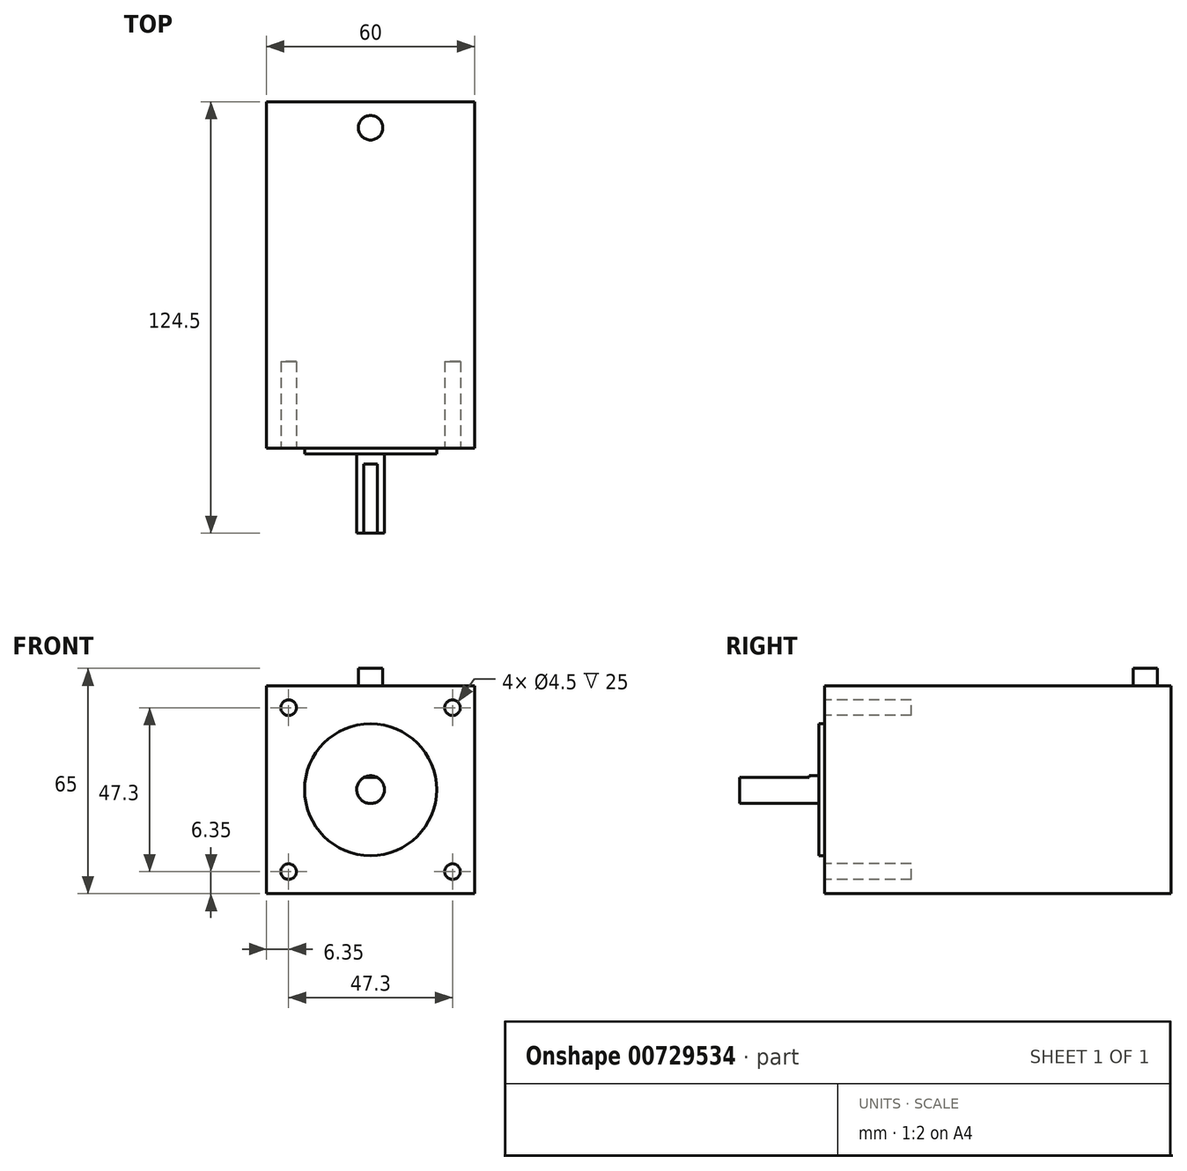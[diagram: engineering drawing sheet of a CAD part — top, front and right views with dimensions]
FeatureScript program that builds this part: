
annotation { "Feature Type Name" : "Feature", "Feature Type Description" : "" }
export const myFeature = defineFeature(function(context is Context, id is Id, definition is map)
    precondition{}
    {
        {
            var Q0;
            Q0=qCreatedBy(makeId("Front.planeOp"),FACE);
            var sketch = newSketch(context, id + "F0", { "sketchPlane" : qUnion([Q0])});
            skLineSegment(sketch, "E0.bottom", {"start": v(-30, 30) * mm, "end": v(30, 30) * mm});
            skLineSegment(sketch, "E0.top", {"start": v(-30, -30) * mm, "end": v(30, -30) * mm});
            skLineSegment(sketch, "E0.left", {"start": v(-30, 30) * mm, "end": v(-30, -30) * mm});
            skLineSegment(sketch, "E0.right", {"start": v(30, 30) * mm, "end": v(30, -30) * mm});
            skPoint(sketch, "E0.middle", {"position": v(0, 0) * mm});
            skCircle(sketch, "E1", {"center": v(0, 0) * mm, "radius": 19.05 * mm});
            skLineSegment(sketch, "E2.bottom", {"start": v(-23.65, 23.65) * mm, "end": v(23.65, 23.65) * mm, "construction": true});
            skLineSegment(sketch, "E2.top", {"start": v(-23.65, -23.65) * mm, "end": v(23.65, -23.65) * mm, "construction": true});
            skLineSegment(sketch, "E2.left", {"start": v(-23.65, 23.65) * mm, "end": v(-23.65, -23.65) * mm, "construction": true});
            skLineSegment(sketch, "E2.right", {"start": v(23.65, 23.65) * mm, "end": v(23.65, -23.65) * mm, "construction": true});
            skCircle(sketch, "E3", {"center": v(0, 0) * mm, "radius": 4 * mm});
            skCircle(sketch, "E4", {"center": v(-23.65, 23.65) * mm, "radius": 2.25 * mm});
            skCircle(sketch, "E5", {"center": v(23.65, 23.65) * mm, "radius": 2.25 * mm});
            skCircle(sketch, "E6", {"center": v(-23.65, -23.65) * mm, "radius": 2.25 * mm});
            skCircle(sketch, "E7", {"center": v(23.65, -23.65) * mm, "radius": 2.25 * mm});
            skSolve(sketch);
        }
        {
            var Q0;
            Q0=makeQuery(id+"F0.imprint","IMPRINT",FACE,{"disambiguationData":[TD([[makeQuery(id+"F0.imprint","IMPRINT",EDGE,{"derivedFrom":sQuery(id+"F0.wireOp",EDGE,"E4")}),1.0]])]});
            var Q1;
            Q1=makeQuery(id+"F0.imprint","IMPRINT",FACE,{"disambiguationData":[TD([[makeQuery(id+"F0.imprint","IMPRINT",EDGE,{"derivedFrom":sQuery(id+"F0.wireOp",EDGE,"E5")}),1.0]])]});
            var Q2;
            Q2=makeQuery(id+"F0.imprint","IMPRINT",FACE,{"disambiguationData":[TD([[makeQuery(id+"F0.imprint","IMPRINT",EDGE,{"derivedFrom":sQuery(id+"F0.wireOp",EDGE,"E7")}),1.0]])]});
            var Q3;
            Q3=makeQuery(id+"F0.imprint","IMPRINT",FACE,{"disambiguationData":[TD([[makeQuery(id+"F0.imprint","IMPRINT",EDGE,{"derivedFrom":sQuery(id+"F0.wireOp",EDGE,"E6")}),1.0]])]});
            var Q4;
            Q4=makeQuery(id+"F0.imprint","IMPRINT",FACE,{"disambiguationData":[TD([[makeQuery(id+"F0.imprint","IMPRINT",EDGE,{"derivedFrom":sQuery(id+"F0.wireOp",EDGE,"E3")}),1.0]])]});
            var Q5;
            Q5=makeQuery(id+"F0.imprint","IMPRINT",FACE,{"disambiguationData":[TD([[makeQuery(id+"F0.imprint","IMPRINT",EDGE,{"derivedFrom":sQuery(id+"F0.wireOp",EDGE,"E1")}),1.0]])]});
            var Q6;
            Q6=makeQuery(id+"F0.imprint","IMPRINT",FACE,{"disambiguationData":[TD([[makeQuery(id+"F0.imprint","IMPRINT",EDGE,{"derivedFrom":sQuery(id+"F0.wireOp",EDGE,"E0.bottom")}),-1.0]])]});
            extrude(context, id + "F1", {"entities" : qUnion([Q0, Q1, Q2, Q3, Q4, Q5, Q6]), "oppositeDirection" : true, "depth" : 100 * mm, "offsetDistance" : 25 * mm});
        }
        {
            var Q0;
            Q0=makeQuery(id+"F0.imprint","IMPRINT",FACE,{"disambiguationData":[TD([[makeQuery(id+"F0.imprint","IMPRINT",EDGE,{"derivedFrom":sQuery(id+"F0.wireOp",EDGE,"E3")}),1.0]])]});
            extrude(context, id + "F2", {"entities" : qUnion([Q0]), "operationType" : NewBodyOperationType.ADD, "depth" : 24.5 * mm, "offsetDistance" : 25 * mm});
        }
        {
            var Q0;
            Q0=makeQuery(id+"F2.opExtrude","CAP_FACE",FACE,{"disambiguationData":[OSD([sQuery(id+"F0.wireOp",EDGE,"E3")])],"isStart":false});
            var sketch = newSketch(context, id + "F3", { "sketchPlane" : qUnion([Q0])});
            skCircle(sketch, "E8", {"center": v(0, 0) * mm, "radius": 4 * mm, "construction": true});
            skLineSegment(sketch, "E9", {"start": v(0, 5.58) * mm, "end": v(0, -4) * mm, "construction": true});
            skLineSegment(sketch, "E10", {"start": v(-1.94, 3.5) * mm, "end": v(1.94, 3.5) * mm});
            skLineSegment(sketch, "E11", {"start": v(0, -4) * mm, "end": v(0, -5.1) * mm, "construction": true});
            skSolve(sketch);
        }
        {
            var Q0;
            {var subQ0=sQuery(id+"F3.wireOp",EDGE,"E10");Q0=makeQuery(id+"F3.imprint","IMPRINT",FACE,{"disambiguationData":[TD([[makeQuery(id+"F3.imprint","IMPRINT",EDGE,{"derivedFrom":subQ0}),1.0]])]});}
            extrude(context, id + "F4", {"entities" : qUnion([Q0]), "operationType" : NewBodyOperationType.REMOVE, "oppositeDirection" : true, "depth" : 20 * mm, "offsetDistance" : 25 * mm});
        }
        {
            var Q0;
            Q0=makeQuery(id+"F0.imprint","IMPRINT",FACE,{"disambiguationData":[TD([[makeQuery(id+"F0.imprint","IMPRINT",EDGE,{"derivedFrom":sQuery(id+"F0.wireOp",EDGE,"E1")}),1.0]])]});
            extrude(context, id + "F5", {"entities" : qUnion([Q0]), "operationType" : NewBodyOperationType.ADD, "depth" : 1.6 * mm, "offsetDistance" : 25 * mm});
        }
        {
            var Q0;
            Q0=makeQuery(id+"F0.imprint","IMPRINT",FACE,{"disambiguationData":[TD([[makeQuery(id+"F0.imprint","IMPRINT",EDGE,{"derivedFrom":sQuery(id+"F0.wireOp",EDGE,"E4")}),1.0]])]});
            var Q1;
            Q1=makeQuery(id+"F0.imprint","IMPRINT",FACE,{"disambiguationData":[TD([[makeQuery(id+"F0.imprint","IMPRINT",EDGE,{"derivedFrom":sQuery(id+"F0.wireOp",EDGE,"E5")}),1.0]])]});
            var Q2;
            Q2=makeQuery(id+"F0.imprint","IMPRINT",FACE,{"disambiguationData":[TD([[makeQuery(id+"F0.imprint","IMPRINT",EDGE,{"derivedFrom":sQuery(id+"F0.wireOp",EDGE,"E7")}),1.0]])]});
            var Q3;
            Q3=makeQuery(id+"F0.imprint","IMPRINT",FACE,{"disambiguationData":[TD([[makeQuery(id+"F0.imprint","IMPRINT",EDGE,{"derivedFrom":sQuery(id+"F0.wireOp",EDGE,"E6")}),1.0]])]});
            extrude(context, id + "F6", {"entities" : qUnion([Q0, Q1, Q2, Q3]), "operationType" : NewBodyOperationType.REMOVE, "oppositeDirection" : true, "depth" : 25 * mm, "offsetDistance" : 25 * mm});
        }
        {
            var Q0;
            Q0=makeQuery(id+"F1.opExtrude","SWEPT_FACE",FACE,{"disambiguationData":[OSD([sQuery(id+"F0.wireOp",EDGE,"E0.bottom")])]});
            var sketch = newSketch(context, id + "F7", { "sketchPlane" : qUnion([Q0])});
            skLineSegment(sketch, "E12", {"start": v(0, 0) * mm, "end": v(0, 114.64) * mm, "construction": true});
            skCircle(sketch, "E13", {"center": v(0, 92.52) * mm, "radius": 3.53 * mm});
            skSolve(sketch);
        }
        {
            var Q0;
            Q0=makeQuery(id+"F7.imprint","IMPRINT",FACE,{"disambiguationData":[TD([[makeQuery(id+"F7.imprint","IMPRINT",EDGE,{"derivedFrom":sQuery(id+"F7.wireOp",EDGE,"E13")}),1.0]])]});
            extrude(context, id + "F8", {"entities" : qUnion([Q0]), "operationType" : NewBodyOperationType.ADD, "depth" : 5 * mm, "offsetDistance" : 25 * mm});
        }
    });
